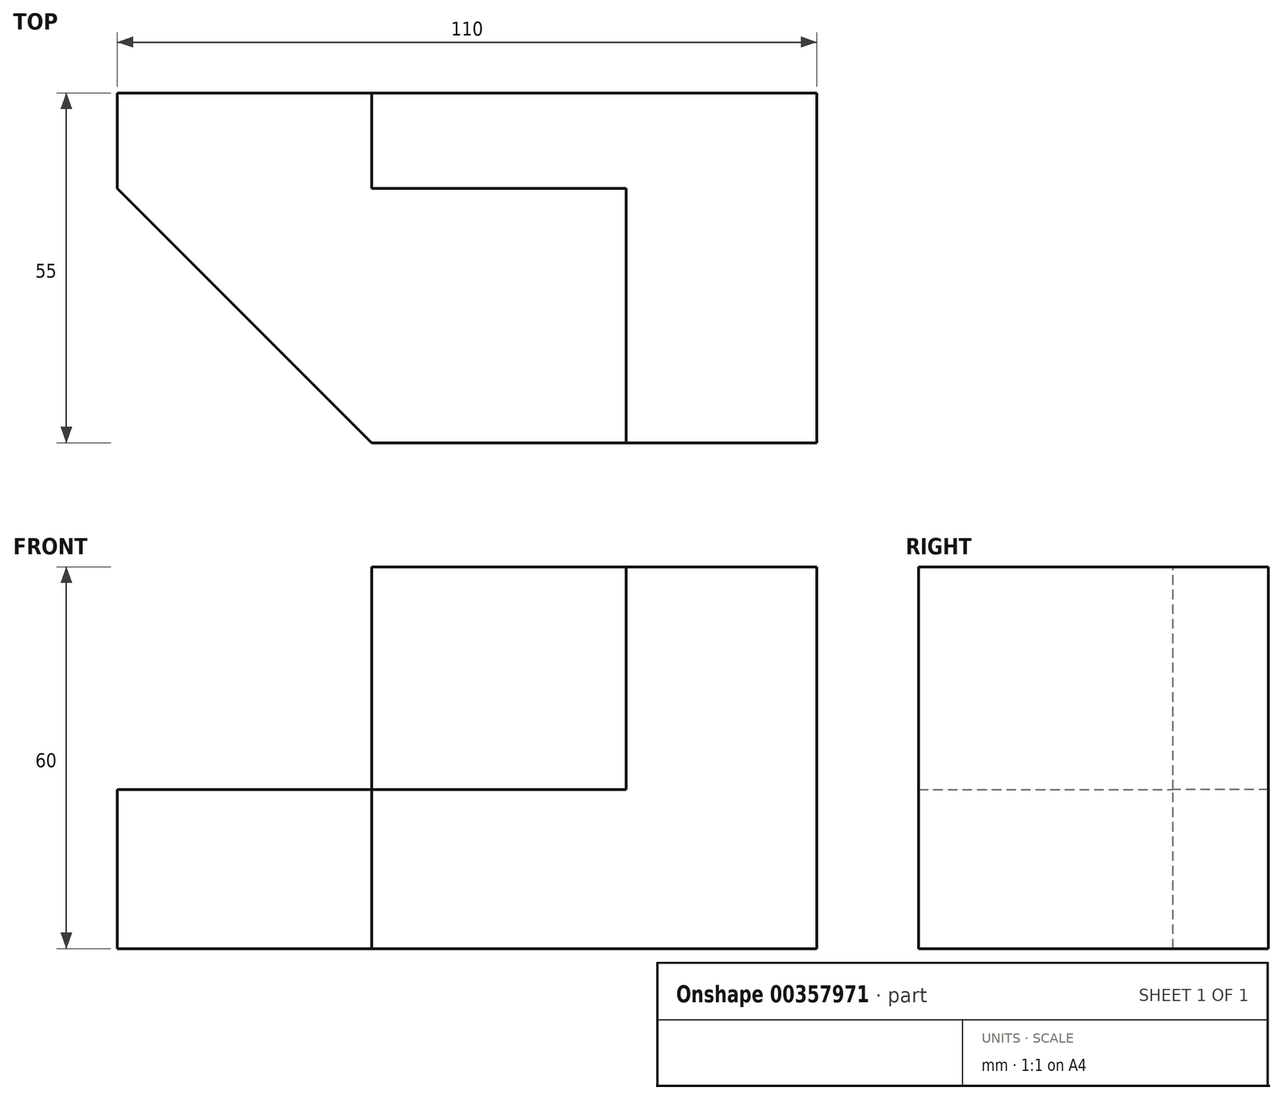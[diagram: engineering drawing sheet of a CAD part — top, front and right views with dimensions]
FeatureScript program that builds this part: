
annotation { "Feature Type Name" : "Feature", "Feature Type Description" : "" }
export const myFeature = defineFeature(function(context is Context, id is Id, definition is map)
    precondition{}
    {
        {
            var Q0;
            Q0=qCreatedBy(makeId("Top.planeOp"),FACE);
            var sketch = newSketch(context, id + "F0", { "sketchPlane" : qUnion([Q0])});
            skLineSegment(sketch, "E0.bottom", {"start": v(-55, 27.5) * mm, "end": v(55, 27.5) * mm});
            skLineSegment(sketch, "E0.top", {"start": v(-55, -27.5) * mm, "end": v(55, -27.5) * mm});
            skLineSegment(sketch, "E0.left", {"start": v(-55, 27.5) * mm, "end": v(-55, -27.5) * mm});
            skLineSegment(sketch, "E0.right", {"start": v(55, 27.5) * mm, "end": v(55, -27.5) * mm});
            skPoint(sketch, "E0.middle", {"position": v(0, 0) * mm});
            skSolve(sketch);
        }
        {
            var Q0;
            Q0 = qSketchRegion(id + "F0", true);
            extrude(context, id + "F1", {"entities" : qUnion([Q0]), "depth" : 60 * mm});
        }
        {
            var Q0;
            Q0=makeQuery(id+"F1.opExtrude","CAP_FACE",FACE,{"disambiguationData":[OSD([sQuery(id+"F0.wireOp",EDGE,"E0.bottom"),sQuery(id+"F0.wireOp",EDGE,"E0.top"),sQuery(id+"F0.wireOp",EDGE,"E0.left"),sQuery(id+"F0.wireOp",EDGE,"E0.right")])],"isStart":false});
            var sketch = newSketch(context, id + "F2", { "sketchPlane" : qUnion([Q0])});
            skLineSegment(sketch, "E1", {"start": v(-55, 12.5) * mm, "end": v(-55, -27.5) * mm});
            skLineSegment(sketch, "E2", {"start": v(-55, -27.5) * mm, "end": v(-15, -27.5) * mm});
            skLineSegment(sketch, "E3", {"start": v(-15, -27.5) * mm, "end": v(-55, 12.5) * mm});
            skSolve(sketch);
        }
        {
            var Q0;
            Q0 = qSketchRegion(id + "F2", true);
            extrude(context, id + "F3", {"entities" : qUnion([Q0]), "operationType" : NewBodyOperationType.REMOVE, "endBound" : BoundingType.THROUGH_ALL, "oppositeDirection" : true, "depth" : 25 * mm});
        }
        {
            var Q0;
            Q0=makeQuery(id+"F1.opExtrude","CAP_FACE",FACE,{"disambiguationData":[OSD([sQuery(id+"F0.wireOp",EDGE,"E0.bottom"),sQuery(id+"F0.wireOp",EDGE,"E0.top"),sQuery(id+"F0.wireOp",EDGE,"E0.left"),sQuery(id+"F0.wireOp",EDGE,"E0.right")])],"isStart":false});
            var sketch = newSketch(context, id + "F4", { "sketchPlane" : qUnion([Q0])});
            skLineSegment(sketch, "E4", {"start": v(25, -27.5) * mm, "end": v(25, 12.5) * mm});
            skLineSegment(sketch, "E5", {"start": v(25, 12.5) * mm, "end": v(-15, 12.5) * mm});
            skLineSegment(sketch, "E6", {"start": v(-15, 12.5) * mm, "end": v(-15, 27.5) * mm});
            skLineSegment(sketch, "E7", {"start": v(-15, 27.5) * mm, "end": v(-55, 27.5) * mm});
            skLineSegment(sketch, "E8", {"start": v(-55, 27.5) * mm, "end": v(-55, 12.5) * mm});
            skLineSegment(sketch, "E9", {"start": v(-55, 12.5) * mm, "end": v(-15, -27.5) * mm});
            skLineSegment(sketch, "E10", {"start": v(-15, -27.5) * mm, "end": v(25, -27.5) * mm});
            skSolve(sketch);
        }
        {
            var Q0;
            Q0=makeQuery(id+"F4.imprint","IMPRINT",FACE,{"disambiguationData":[TD([[makeQuery(id+"F4.imprint","IMPRINT",EDGE,{"derivedFrom":sQuery(id+"F4.wireOp",EDGE,"E4")}),1.0]])]});
            extrude(context, id + "F5", {"entities" : qUnion([Q0]), "operationType" : NewBodyOperationType.REMOVE, "oppositeDirection" : true, "depth" : 35 * mm});
        }
    });
